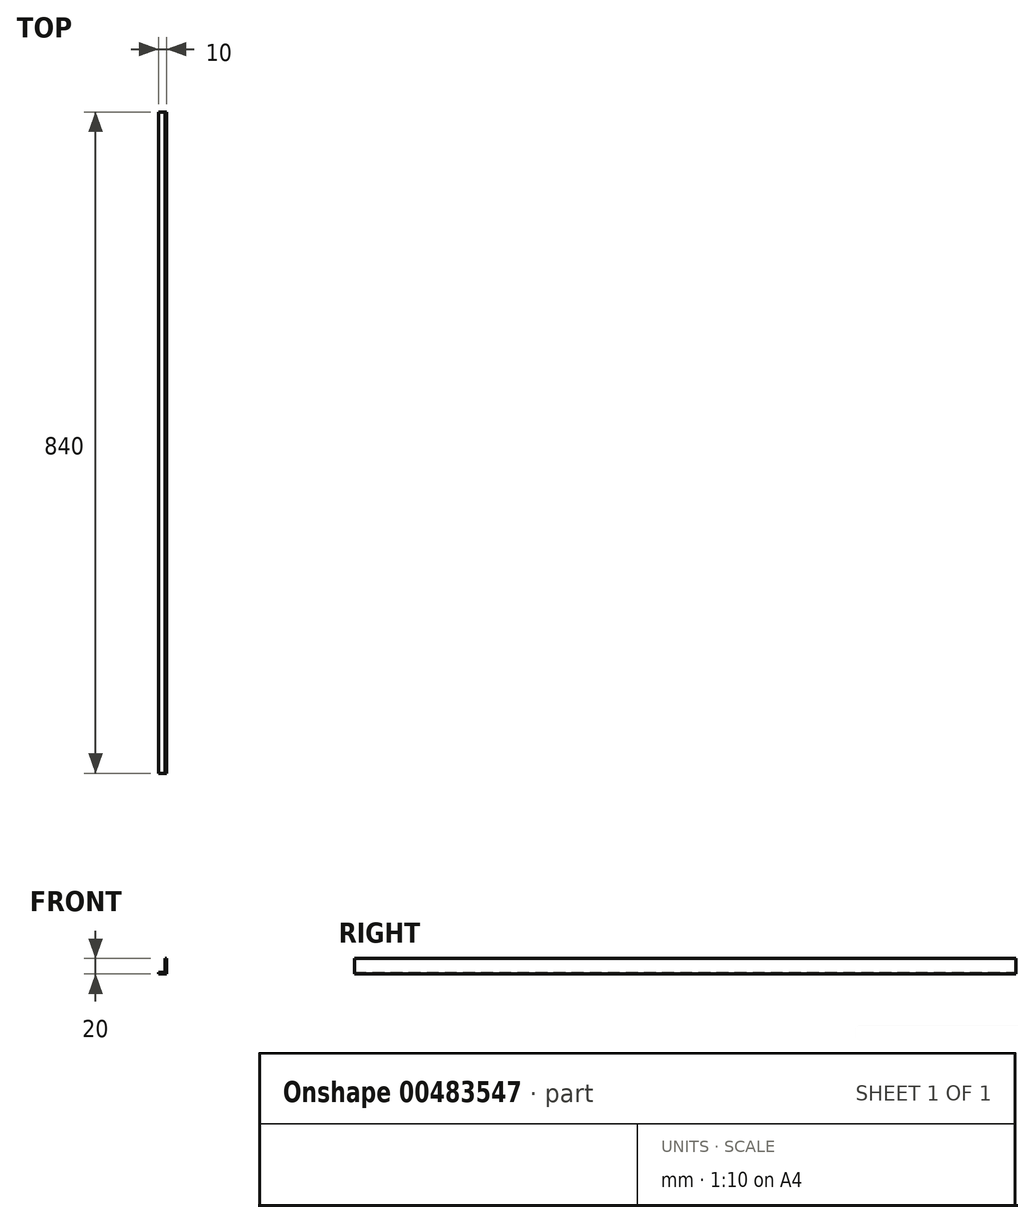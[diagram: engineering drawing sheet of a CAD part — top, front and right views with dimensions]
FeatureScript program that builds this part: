
annotation { "Feature Type Name" : "Feature", "Feature Type Description" : "" }
export const myFeature = defineFeature(function(context is Context, id is Id, definition is map)
    precondition{}
    {
        {
            var Q0;
            Q0=qCreatedBy(makeId("Front.planeOp"),FACE);
            var sketch = newSketch(context, id + "F0", { "sketchPlane" : qUnion([Q0])});
            skLineSegment(sketch, "E0", {"start": v(0, 0) * mm, "end": v(10, 0) * mm});
            skLineSegment(sketch, "E1", {"start": v(10, 0) * mm, "end": v(10, 20) * mm});
            skLineSegment(sketch, "E2", {"start": v(10, 20) * mm, "end": v(8, 20) * mm});
            skLineSegment(sketch, "E3", {"start": v(8, 20) * mm, "end": v(8, 2) * mm});
            skLineSegment(sketch, "E4", {"start": v(8, 2) * mm, "end": v(0, 2) * mm});
            skLineSegment(sketch, "E5", {"start": v(0, 2) * mm, "end": v(0, 0) * mm});
            skSolve(sketch);
        }
        {
            var Q0;
            Q0=qSketchRegion(id+"F0",true);
            extrude(context, id + "F1", {"entities" : qUnion([Q0]), "depth" : 840 * mm});
        }
    });
